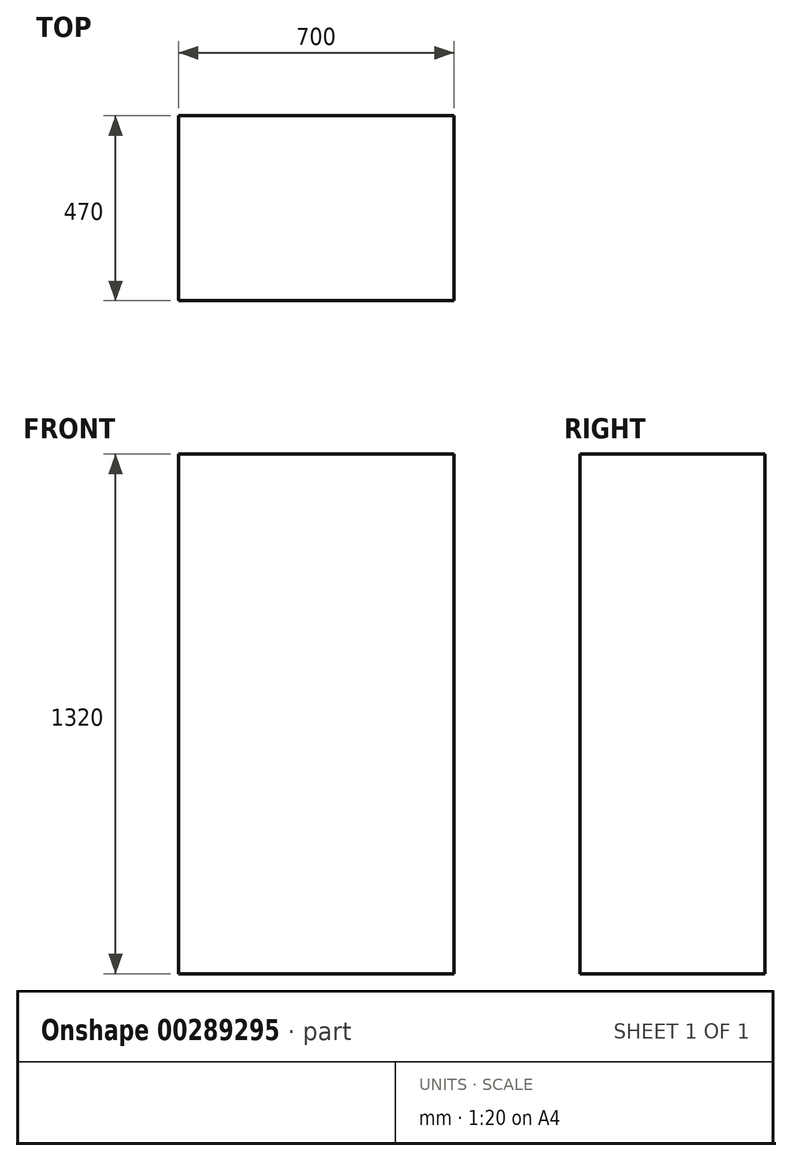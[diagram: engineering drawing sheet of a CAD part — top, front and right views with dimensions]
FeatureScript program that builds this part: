
annotation { "Feature Type Name" : "Feature", "Feature Type Description" : "" }
export const myFeature = defineFeature(function(context is Context, id is Id, definition is map)
    precondition{}
    {
        {
            var Q0;
            Q0=qCreatedBy(makeId("Top.planeOp"),FACE);
            var sketch = newSketch(context, id + "F0", { "sketchPlane" : qUnion([Q0])});
            skLineSegment(sketch, "E0.bottom", {"start": v(350, -235) * mm, "end": v(-350, -235) * mm});
            skLineSegment(sketch, "E0.top", {"start": v(350, 235) * mm, "end": v(-350, 235) * mm});
            skLineSegment(sketch, "E0.left", {"start": v(350, -235) * mm, "end": v(350, 235) * mm});
            skLineSegment(sketch, "E0.right", {"start": v(-350, -235) * mm, "end": v(-350, 235) * mm});
            skPoint(sketch, "E0.middle", {"position": v(0, 0) * mm});
            skPoint(sketch, "E1.middle", {"position": v(-350, 0) * mm});
            skSolve(sketch);
        }
        {
            var Q0;
            Q0=makeQuery(id+"F0.imprint","IMPRINT",FACE,{"disambiguationData":[TD([[makeQuery(id+"F0.imprint","IMPRINT",EDGE,{"derivedFrom":sQuery(id+"F0.wireOp",EDGE,"E0.bottom")}),-1.0]])]});
            extrude(context, id + "F1", {"entities" : qUnion([Q0]), "depth" : 1320 * mm});
        }
    });
